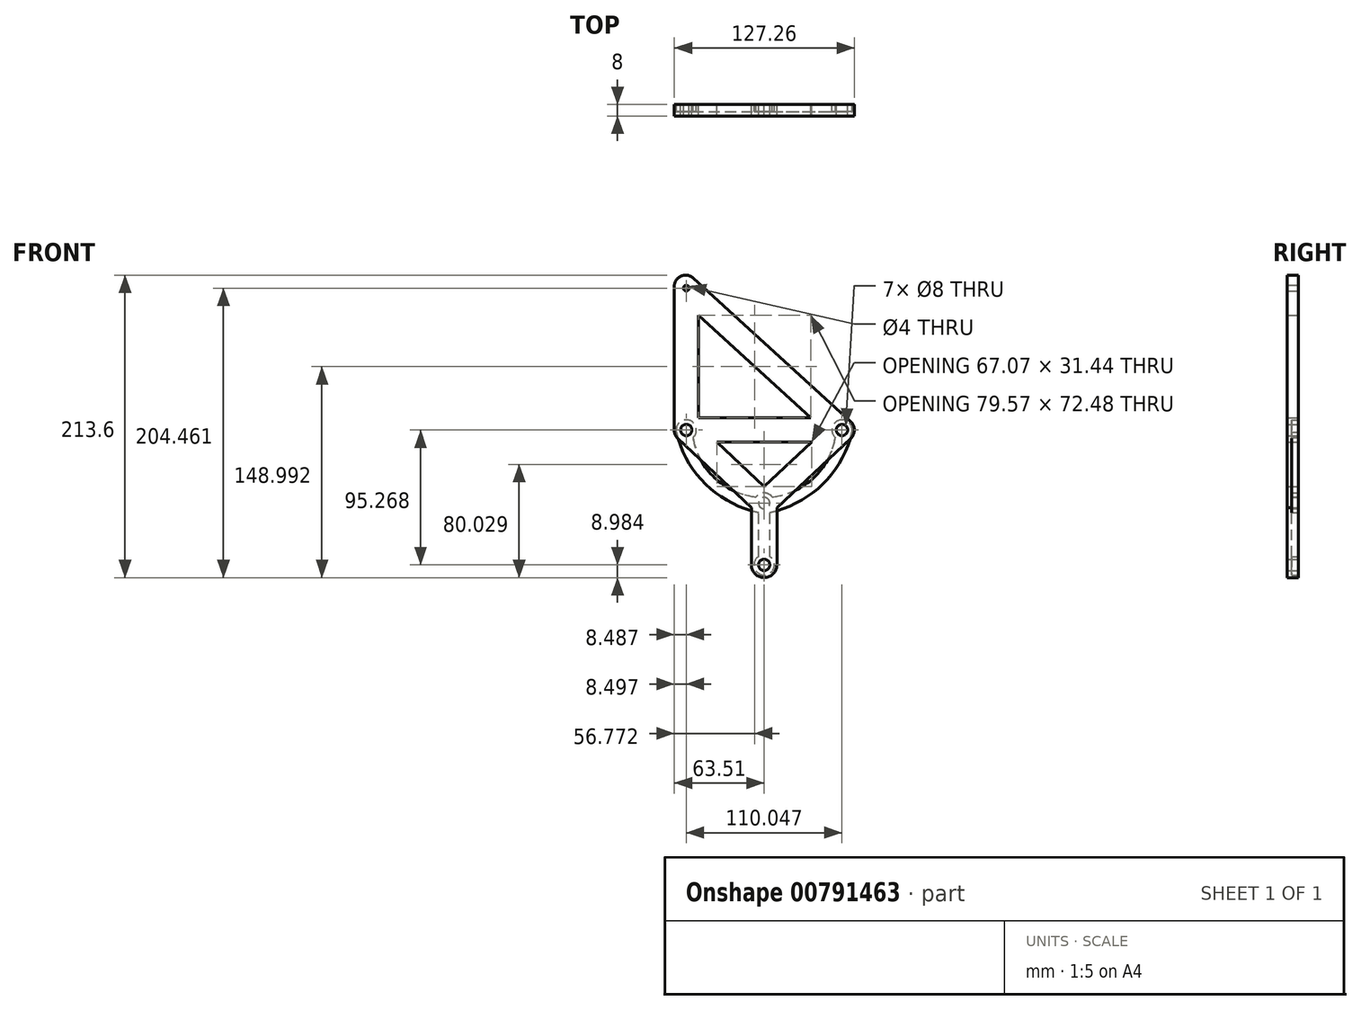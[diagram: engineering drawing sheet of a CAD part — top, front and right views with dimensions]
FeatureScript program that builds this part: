
annotation { "Feature Type Name" : "Feature", "Feature Type Description" : "" }
export const myFeature = defineFeature(function(context is Context, id is Id, definition is map)
    precondition{}
    {
        {
            var Q0;
            Q0=qCreatedBy(makeId("Front.planeOp"),FACE);
            var sketch = newSketch(context, id + "F0", { "sketchPlane" : qUnion([Q0])});
            skLineSegment(sketch, "E0", {"start": v(0, -97.74) * mm, "end": v(0, -54.07) * mm, "construction": true});
            skLineSegment(sketch, "E1", {"start": v(0, -54.07) * mm, "end": v(-55.02, -2.48) * mm, "construction": true});
            skLineSegment(sketch, "E2", {"start": v(-55.02, -2.48) * mm, "end": v(55.02, -2.48) * mm, "construction": true});
            skLineSegment(sketch, "E3", {"start": v(55.02, -2.48) * mm, "end": v(0, -54.08) * mm, "construction": true});
            skLineSegment(sketch, "E4", {"start": v(-55.01, -2.49) * mm, "end": v(-55.01, 97.73) * mm, "construction": true});
            skLineSegment(sketch, "E5", {"start": v(-55, 97.72) * mm, "end": v(55, -2.48) * mm, "construction": true});
            skLineSegment(sketch, "E6.0", {"start": v(-63.51, -6.17) * mm, "end": v(-63.51, 116.97) * mm});
            skLineSegment(sketch, "E6.1", {"start": v(0, -65.73) * mm, "end": v(-63.51, -6.17) * mm});
            skLineSegment(sketch, "E6.2", {"start": v(67.54, -2.4) * mm, "end": v(0, -65.73) * mm});
            skLineSegment(sketch, "E6.3", {"start": v(-63.51, 116.97) * mm, "end": v(67.54, -2.4) * mm});
            skCircle(sketch, "E7", {"center": v(-55.02, -2.48) * mm, "radius": 4 * mm});
            skCircle(sketch, "E8", {"center": v(55.02, -2.48) * mm, "radius": 4 * mm});
            skCircle(sketch, "E9", {"center": v(-55.01, 97.73) * mm, "radius": 2 * mm});
            skCircle(sketch, "E10", {"center": v(0, -97.74) * mm, "radius": 4 * mm});
            skLineSegment(sketch, "E11", {"start": v(9, -97.74) * mm, "end": v(9, -57.3) * mm});
            skLineSegment(sketch, "E12", {"start": v(-9, -97.74) * mm, "end": v(-9, -57.29) * mm});
            skArc(sketch, "E13", {"start": v(-9, -97.74) * mm, "mid": v(0, -106.73) * mm, "end": v(9, -97.74) * mm});
            skLineSegment(sketch, "E14", {"start": v(-46.52, 6.02) * mm, "end": v(-46.52, 78.5) * mm});
            skLineSegment(sketch, "E15", {"start": v(-46.52, 78.5) * mm, "end": v(33.05, 6.02) * mm});
            skLineSegment(sketch, "E16", {"start": v(33.05, 6.02) * mm, "end": v(-46.52, 6.02) * mm});
            skLineSegment(sketch, "E17", {"start": v(-33.53, -10.98) * mm, "end": v(33.53, -10.98) * mm});
            skLineSegment(sketch, "E18", {"start": v(33.53, -10.98) * mm, "end": v(0, -42.42) * mm});
            skLineSegment(sketch, "E19", {"start": v(0, -42.42) * mm, "end": v(-33.53, -10.98) * mm});
            skSolve(sketch);
        }
        {
            var Q0;
            Q0 = qSketchRegion(id + "F0", true);
            extrude(context, id + "F1", {"entities" : qUnion([Q0]), "depth" : 8 * mm, "offsetDistance" : 25 * mm});
        }
        {
            var Q0;
            Q0=makeQuery(id+"F1.opExtrude","SWEPT_EDGE",EDGE,{"disambiguationData":[OSD([sQuery(id+"F0.wireOp",EDGE,"E6.0"),sQuery(id+"F0.wireOp",EDGE,"E6.1")])]});
            var Q1;
            Q1=makeQuery(id+"F1.opExtrude","SWEPT_EDGE",EDGE,{"disambiguationData":[OSD([sQuery(id+"F0.wireOp",EDGE,"E6.2"),sQuery(id+"F0.wireOp",EDGE,"E6.3")])]});
            var Q2;
            Q2=makeQuery(id+"F1.opExtrude","SWEPT_EDGE",EDGE,{"disambiguationData":[OSD([sQuery(id+"F0.wireOp",EDGE,"E6.0"),sQuery(id+"F0.wireOp",EDGE,"E6.3")])]});
            fillet(context, id + "F2", {"entities" : qUnion([Q0, Q1, Q2]), "radius" : 8 * mm, "tangentPropagation" : true, "allowEdgeOverflow" : false});
        }
        {
            var Q0;
            Q0=qCreatedBy(makeId("Front.planeOp"),FACE);
            var sketch = newSketch(context, id + "F3", { "sketchPlane" : qUnion([Q0])});
            skArc(sketch, "E20", {"start": v(-4, -91.8) * mm, "mid": v(0.02, -104.91) * mm, "end": v(4, -91.8) * mm});
            skArc(sketch, "E21", {"start": v(5.71, -49.75) * mm, "mid": v(0, -46.9) * mm, "end": v(-5.72, -49.75) * mm});
            skArc(sketch, "E22", {"start": v(-50.35, -7.9) * mm, "mid": v(-52.75, 4.32) * mm, "end": v(-62.03, -4) * mm});
            skCircle(sketch, "E23", {"center": v(0, -54.07) * mm, "radius": 4 * mm});
            skCircle(sketch, "E24", {"center": v(0, -97.75) * mm, "radius": 4 * mm});
            skCircle(sketch, "E25", {"center": v(-55.02, -2.48) * mm, "radius": 4 * mm});
            skLineSegment(sketch, "E26", {"start": v(4, -91.81) * mm, "end": v(4, -60.67) * mm});
            skLineSegment(sketch, "E27", {"start": v(-4, -91.8) * mm, "end": v(-4, -60.67) * mm});
            skArc(sketch, "E28", {"start": v(-62.03, -4) * mm, "mid": v(-41.27, -40.78) * mm, "end": v(-4, -60.67) * mm});
            skArc(sketch, "E29", {"start": v(-50.35, -7.9) * mm, "mid": v(-34.99, -36.24) * mm, "end": v(-5.72, -49.75) * mm});
            skArc(sketch, "E30", {"start": v(4, -60.67) * mm, "mid": v(41.27, -40.79) * mm, "end": v(62.03, -4) * mm});
            skArc(sketch, "E31", {"start": v(5.71, -49.75) * mm, "mid": v(34.98, -36.25) * mm, "end": v(50.35, -7.9) * mm});
            skCircle(sketch, "E32", {"center": v(55.02, -2.48) * mm, "radius": 4 * mm});
            skArc(sketch, "E33", {"start": v(62.03, -4) * mm, "mid": v(52.75, 4.32) * mm, "end": v(50.35, -7.9) * mm});
            skLineSegment(sketch, "E34", {"start": v(0, -54.07) * mm, "end": v(55.02, -2.48) * mm, "construction": true});
            skLineSegment(sketch, "E35", {"start": v(0, -54.07) * mm, "end": v(-55.02, -2.48) * mm, "construction": true});
            skLineSegment(sketch, "E36", {"start": v(0, -54.07) * mm, "end": v(0, -97.74) * mm, "construction": true});
            skSolve(sketch);
        }
        {
            var Q0;
            Q0 = qSketchRegion(id + "F3", true);
            extrude(context, id + "F4", {"entities" : qUnion([Q0]), "depth" : 5 * mm, "offsetDistance" : 25 * mm});
        }
    });
